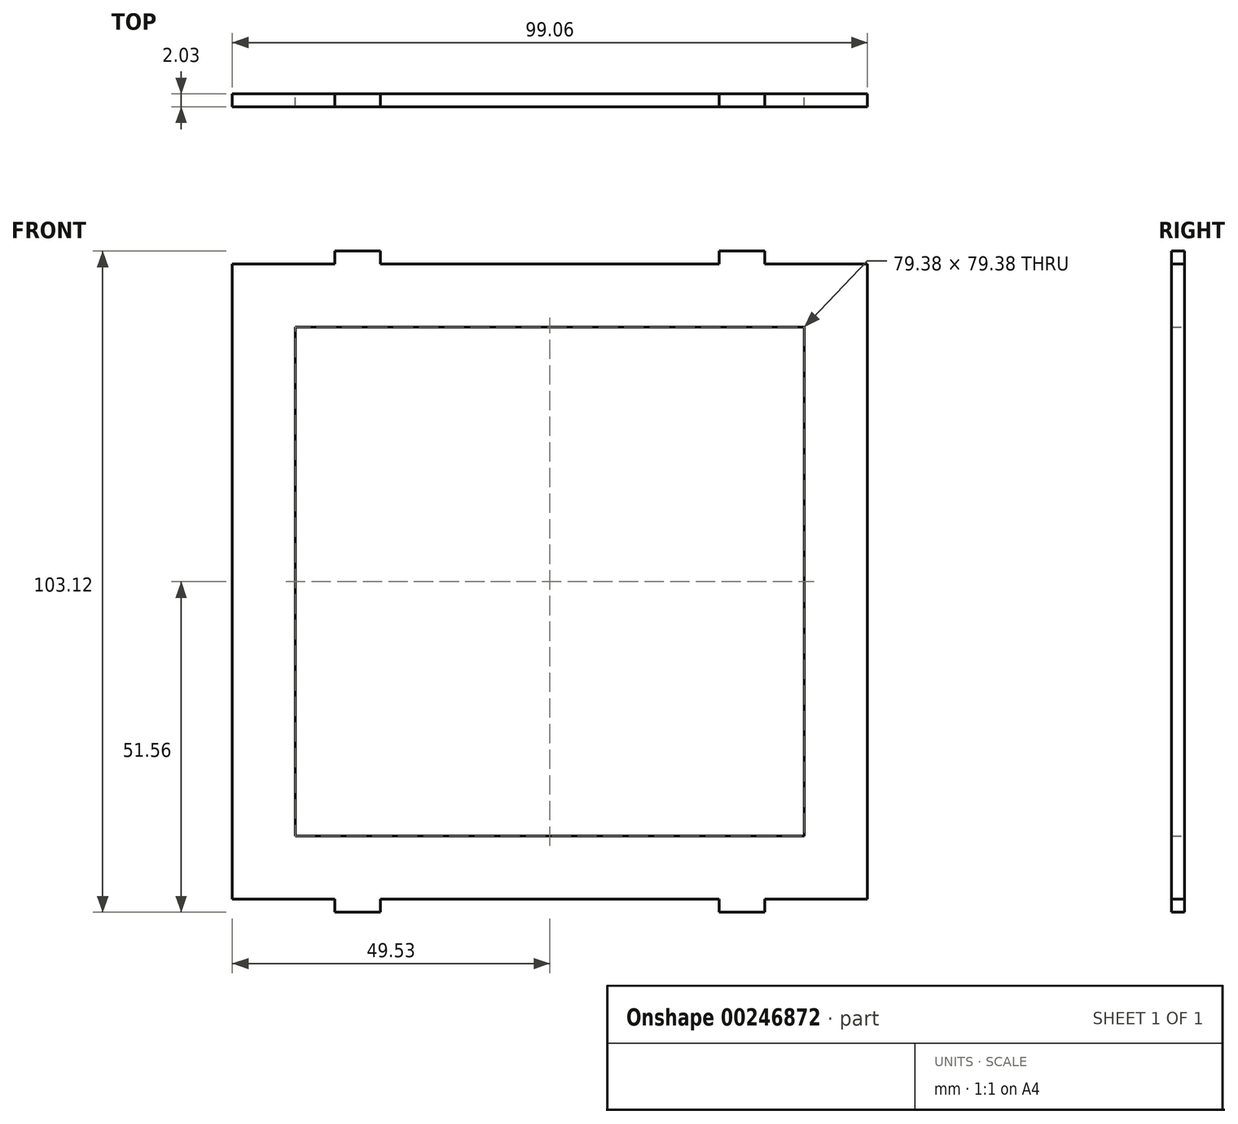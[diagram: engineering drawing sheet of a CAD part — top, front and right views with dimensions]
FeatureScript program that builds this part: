
annotation { "Feature Type Name" : "Feature", "Feature Type Description" : "" }
export const myFeature = defineFeature(function(context is Context, id is Id, definition is map)
    precondition{}
    {
        {
            var Q0;
            Q0=qCreatedBy(makeId("Front.planeOp"),FACE);
            var sketch = newSketch(context, id + "F0", { "sketchPlane" : qUnion([Q0])});
            skLineSegment(sketch, "E0.bottom", {"start": v(-39.69, 39.69) * mm, "end": v(39.69, 39.69) * mm});
            skLineSegment(sketch, "E0.top", {"start": v(-39.69, -39.69) * mm, "end": v(39.69, -39.69) * mm});
            skLineSegment(sketch, "E0.left", {"start": v(-39.69, 39.69) * mm, "end": v(-39.69, -39.69) * mm});
            skLineSegment(sketch, "E0.right", {"start": v(39.69, 39.69) * mm, "end": v(39.69, -39.69) * mm});
            skPoint(sketch, "E0.middle", {"position": v(0, 0) * mm});
            skLineSegment(sketch, "E1.0", {"start": v(-49.53, 49.53) * mm, "end": v(-33.53, 49.53) * mm});
            skLineSegment(sketch, "E1.1", {"start": v(-49.53, 49.53) * mm, "end": v(-49.53, 0) * mm});
            skLineSegment(sketch, "E1.2", {"start": v(-49.53, -49.53) * mm, "end": v(-33.53, -49.53) * mm});
            skLineSegment(sketch, "E1.3", {"start": v(49.53, 49.53) * mm, "end": v(49.53, 0) * mm});
            skLineSegment(sketch, "E2.top", {"start": v(-33.53, 51.56) * mm, "end": v(-26.42, 51.56) * mm});
            skLineSegment(sketch, "E2.left", {"start": v(-33.53, 49.53) * mm, "end": v(-33.53, 51.56) * mm});
            skLineSegment(sketch, "E2.right", {"start": v(-26.42, 49.53) * mm, "end": v(-26.42, 51.56) * mm});
            skLineSegment(sketch, "E3", {"start": v(0, 49.53) * mm, "end": v(0, 72.46) * mm, "construction": true});
            skLineSegment(sketch, "E4.trimOffspring", {"start": v(-26.42, 49.53) * mm, "end": v(26.42, 49.53) * mm});
            skLineSegment(sketch, "E5.MirrorCS", {"start": v(26.42, 49.53) * mm, "end": v(26.42, 51.56) * mm});
            skLineSegment(sketch, "E6.MirrorCS", {"start": v(33.53, 51.56) * mm, "end": v(26.42, 51.56) * mm});
            skLineSegment(sketch, "E7.MirrorCS", {"start": v(33.53, 49.53) * mm, "end": v(33.53, 51.56) * mm});
            skLineSegment(sketch, "E8.trimOffspring", {"start": v(33.53, 49.53) * mm, "end": v(49.53, 49.53) * mm});
            skLineSegment(sketch, "E9.trimOffspring", {"start": v(-49.53, 0) * mm, "end": v(-49.53, 0) * mm});
            skLineSegment(sketch, "E10", {"start": v(-49.53, 0) * mm, "end": v(-94.59, 0) * mm, "construction": true});
            skLineSegment(sketch, "E11.trimOffspring", {"start": v(-49.53, 0) * mm, "end": v(-49.53, -49.53) * mm});
            skLineSegment(sketch, "E12.MirrorCS", {"start": v(-26.42, -49.53) * mm, "end": v(-26.42, -51.56) * mm});
            skLineSegment(sketch, "E13.MirrorCS", {"start": v(-33.53, -51.56) * mm, "end": v(-26.42, -51.56) * mm});
            skLineSegment(sketch, "E14.MirrorCS", {"start": v(-33.53, -49.53) * mm, "end": v(-33.53, -51.56) * mm});
            skLineSegment(sketch, "E15.MirrorCS", {"start": v(33.53, -49.53) * mm, "end": v(33.53, -51.56) * mm});
            skLineSegment(sketch, "E16.MirrorCS", {"start": v(33.53, -51.56) * mm, "end": v(26.42, -51.56) * mm});
            skLineSegment(sketch, "E17.MirrorCS", {"start": v(26.42, -49.53) * mm, "end": v(26.42, -51.56) * mm});
            skLineSegment(sketch, "E18.trimOffspring", {"start": v(-26.42, -49.53) * mm, "end": v(26.42, -49.53) * mm});
            skLineSegment(sketch, "E19.trimOffspring", {"start": v(33.53, -49.53) * mm, "end": v(49.53, -49.53) * mm});
            skLineSegment(sketch, "E20.trimOffspring", {"start": v(49.53, 0) * mm, "end": v(49.53, -49.53) * mm});
            skSolve(sketch);
        }
        {
            var Q0;
            Q0=makeQuery(id+"F0.imprint","IMPRINT",FACE,{"disambiguationData":[TD([[makeQuery(id+"F0.imprint","IMPRINT",EDGE,{"derivedFrom":sQuery(id+"F0.wireOp",EDGE,"E0.bottom")}),1.0]])]});
            extrude(context, id + "F1", {"entities" : qUnion([Q0]), "depth" : 2.03 * mm});
        }
    });
